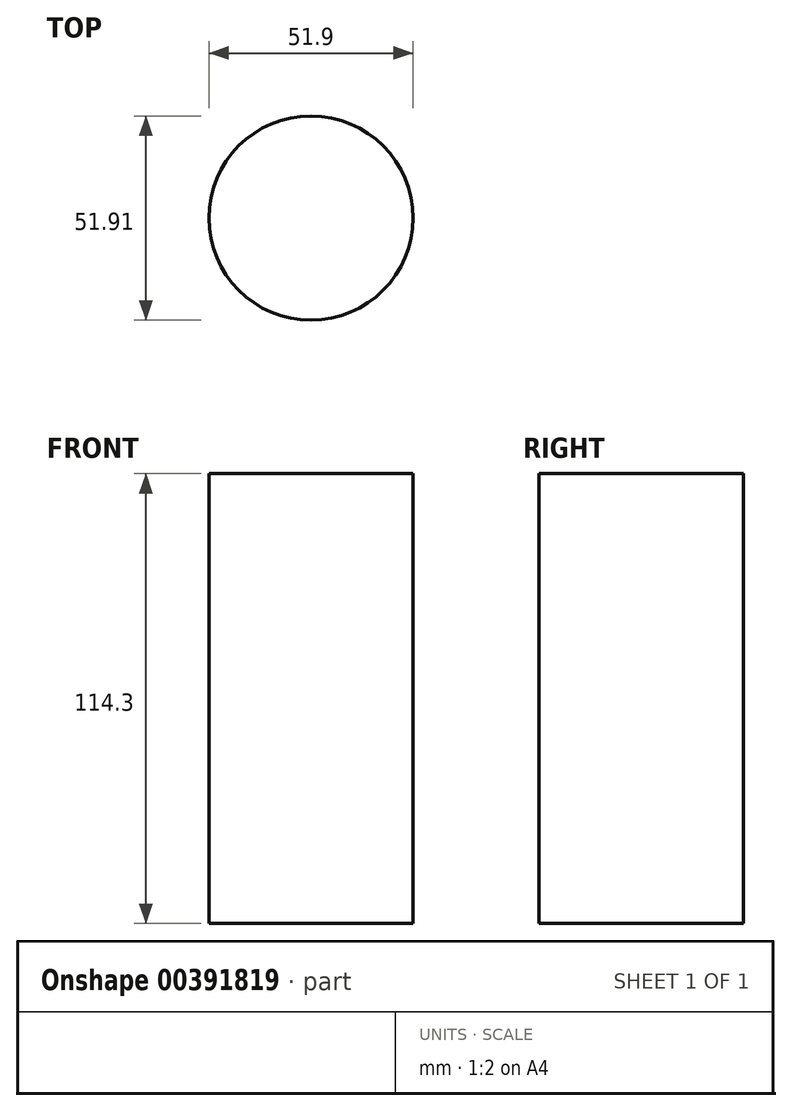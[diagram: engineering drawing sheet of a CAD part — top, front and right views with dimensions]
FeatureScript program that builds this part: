
annotation { "Feature Type Name" : "Feature", "Feature Type Description" : "" }
export const myFeature = defineFeature(function(context is Context, id is Id, definition is map)
    precondition{}
    {
        {
            var Q0;
            Q0=qCreatedBy(makeId("Top.planeOp"),FACE);
            var sketch = newSketch(context, id + "F0", { "sketchPlane" : qUnion([Q0])});
            skCircle(sketch, "E0", {"center": v(-10.94, 46.95) * mm, "radius": 25.95 * mm});
            skSolve(sketch);
        }
        {
            var Q0;
            Q0=makeQuery(id+"F0.imprint","IMPRINT",FACE,{"disambiguationData":[TD([[makeQuery(id+"F0.imprint","IMPRINT",EDGE,{"derivedFrom":sQuery(id+"F0.wireOp",EDGE,"E0")}),1.0]])]});
            extrude(context, id + "F1", {"entities" : qUnion([Q0]), "depth" : 114.3 * mm, "offsetDistance" : 25.4 * mm});
        }
        {
            var Q0;
            Q0 = qSketchRegion(id + "F0", true);
            extrude(context, id + "F2", {"entities" : qUnion([Q0]), "operationType" : NewBodyOperationType.ADD, "depth" : 25.4 * mm, "offsetDistance" : 25.4 * mm});
        }
    });
